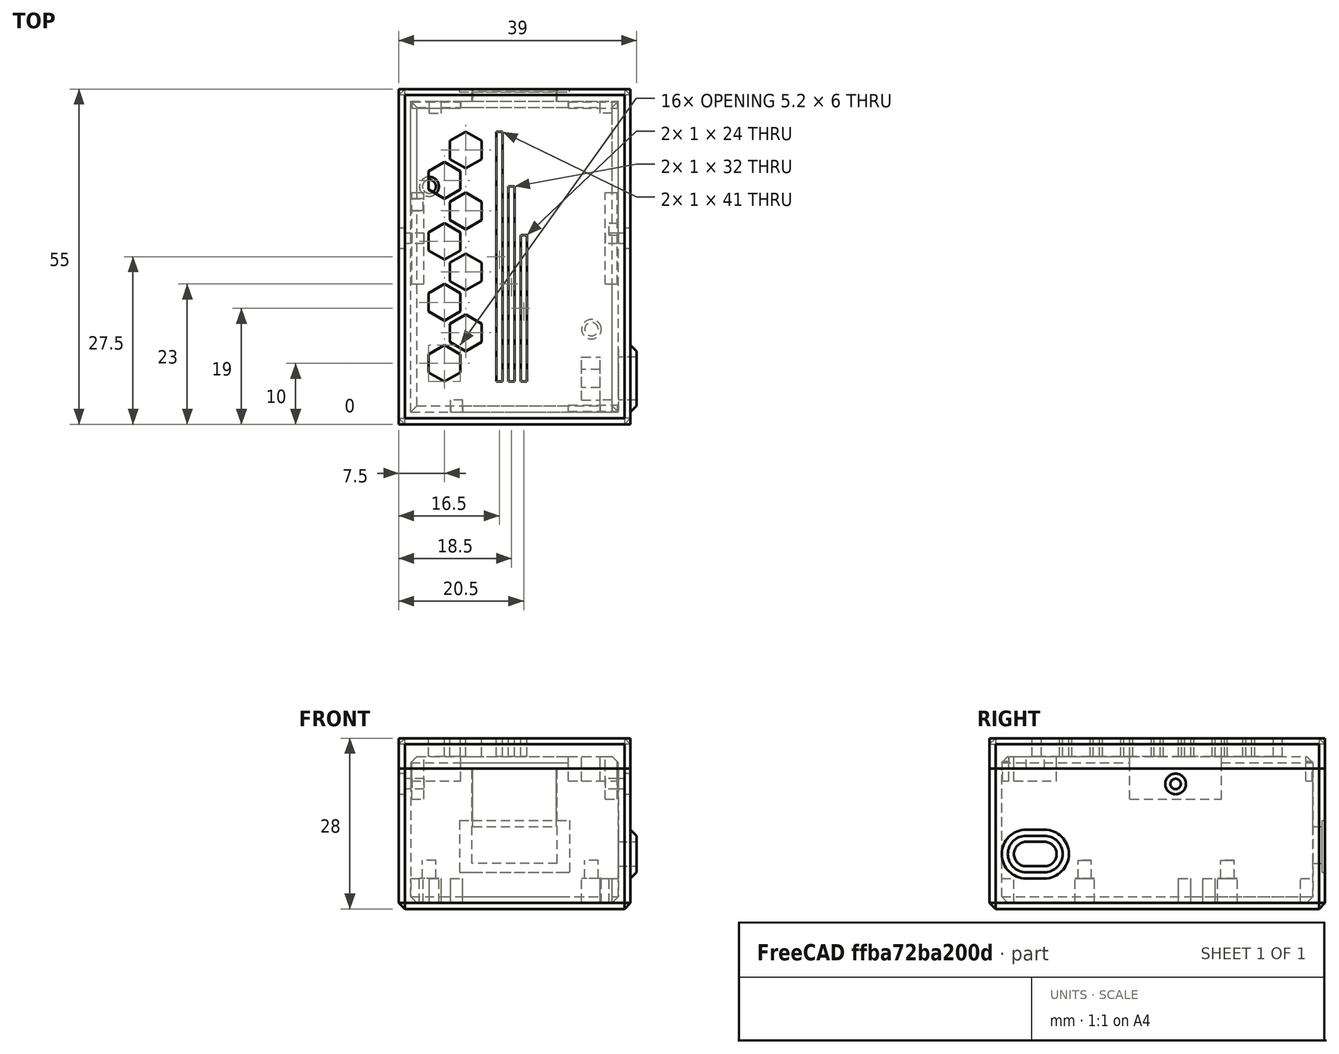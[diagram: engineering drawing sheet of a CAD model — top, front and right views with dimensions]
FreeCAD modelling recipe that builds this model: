
FCSTD DOCUMENT  (FreeCAD 0.18R16146 (Git))
Label: ac-dc5v-mounter
License: All rights reserved
LicenseURL: http://en.wikipedia.org/wiki/All_rights_reserved
objects: Part::Box×38, Part::MultiFuse×20, Part::Cylinder×13, Part::Feature×11, Part::Cut×9, Part::Chamfer×6
note: 97 computed .brp shape members not serialized (recipe doc carries the construction recipe); baked Part::Feature solids carry a one-line shape summary decoded from their .brp

FEATURE [Part::Box] Box  label="Cube"
  AttacherType = Attacher::AttachEngine3D
  Height = 1
  Length = 34
  Width = 51
FEATURE [Part::Box] Box001  label="Cube001"
  AttacherType = Attacher::AttachEngine3D
  Height = 5
  Length = 2
  Placement = pos=(6.5,0,0) rot=(0,0,1;0rad)
  Width = 2
FEATURE [Part::Box] Box002  label="Cube002"
  AttacherType = Attacher::AttachEngine3D
  Height = 5
  Length = 2
  Placement = pos=(0,33,0) rot=(0,0,1;0rad)
  Width = 2
FEATURE [Part::Box] Box003  label="Cube003"
  AttacherType = Attacher::AttachEngine3D
  Height = 5
  Length = 2
  Placement = pos=(31,0,0) rot=(0,0,1;0rad)
  Width = 2
FEATURE [Part::Box] Box004  label="Cube004"
  AttacherType = Attacher::AttachEngine3D
  Height = 5
  Length = 2
  Placement = pos=(31,49,0) rot=(0,0,1;0rad)
  Width = 2
FEATURE [Part::Box] Box005  label="Cube005"
  AttacherType = Attacher::AttachEngine3D
  Height = 5
  Length = 2
  Placement = pos=(3,49,0) rot=(0,0,1;0rad)
  Width = 2
FEATURE [Part::Box] Box006  label="Cube006"
  AttacherType = Attacher::AttachEngine3D
  Height = 5
  Length = 1.5
  Placement = pos=(32.5,29,0) rot=(0,0,1;0rad)
  Width = 2
FEATURE [Part::Box] Box007  label="Cube007"
  AttacherType = Attacher::AttachEngine3D
  Height = 23
  Length = 2
  Placement = pos=(-2,-2,0) rot=(0,0,1;0rad)
  Width = 55
FEATURE [Part::MultiFuse] Fusion
  Shapes = -> [Box006,Box005,Box004,Box003,Box002,Box001]
FEATURE [Part::Box] Box008  label="Cube008"
  AttacherType = Attacher::AttachEngine3D
  Height = 23
  Length = 38
  Placement = pos=(-2,-2,0) rot=(0,0,1;0rad)
  Width = 2
FEATURE [Part::Box] Box009  label="Cube009"
  AttacherType = Attacher::AttachEngine3D
  Height = 23
  Length = 12
  Placement = pos=(-2,51,0) rot=(0,0,1;0rad)
  Width = 2
FEATURE [Part::Box] Box010  label="Cube010"
  AttacherType = Attacher::AttachEngine3D
  Height = 23
  Length = 2
  Placement = pos=(34,-2,0) rot=(0,0,1;0rad)
  Width = 55
FEATURE [Part::Cylinder] Cylinder
  Angle = 360
  AttacherType = Attacher::AttachEngine3D
  Height = 5
  Placement = pos=(3,37,0) rot=(0,0,1;0rad)
  Radius = 1.6
FEATURE [Part::Cylinder] Cylinder001
  Angle = 360
  AttacherType = Attacher::AttachEngine3D
  Height = 5
  Placement = pos=(29.6,13.6,0) rot=(0,0,1;0rad)
  Radius = 1.6
FEATURE [Part::Cylinder] Cylinder002
  Angle = 360
  AttacherType = Attacher::AttachEngine3D
  Height = 8
  Placement = pos=(29.6,13.6,0) rot=(0,0,1;0rad)
  Radius = 1.1
FEATURE [Part::Cylinder] Cylinder003
  Angle = 360
  AttacherType = Attacher::AttachEngine3D
  Height = 8
  Placement = pos=(3,37,0) rot=(0,0,1;0rad)
  Radius = 1.1
FEATURE [Part::Box] Box011  label="Cube011"
  AttacherType = Attacher::AttachEngine3D
  Height = 23
  Length = 12
  Placement = pos=(24,51,0) rot=(0,0,1;0rad)
  Width = 2
FEATURE [Part::Box] Box012  label="Cube012"
  AttacherType = Attacher::AttachEngine3D
  Height = 7.5
  Length = 15
  Placement = pos=(9.5,51,0) rot=(0,0,1;0rad)
  Width = 2
FEATURE [Part::Box] Box013  label="Cube013"
  AttacherType = Attacher::AttachEngine3D
  Height = 8.5
  Length = 18
  Placement = pos=(8,52.5,6) rot=(0,0,1;0rad)
  Width = 2
FEATURE [Part::Box] Box014  label="Cube014"
  AttacherType = Attacher::AttachEngine3D
  Height = 2
  Length = 8
  Placement = pos=(0.15,49.85,25) rot=(0,0,1;0rad)
  Width = 1
FEATURE [Part::Box] Box015  label="Cube015"
  AttacherType = Attacher::AttachEngine3D
  Height = 2
  Length = 8
  Placement = pos=(25.85,49.85,25) rot=(0,0,1;0rad)
  Width = 1
FEATURE [Part::Box] Box016  label="Cube016"
  AttacherType = Attacher::AttachEngine3D
  Height = 5
  Length = 2
  Placement = pos=(0.15,21,22) rot=(0,0,1;0rad)
  Width = 15
FEATURE [Part::Box] Box017  label="Cube017"
  AttacherType = Attacher::AttachEngine3D
  Height = 5
  Length = 2
  Placement = pos=(31.85,21,22) rot=(0,0,1;0rad)
  Width = 15
FEATURE [Part::Box] Box018  label="Cube018"
  AttacherType = Attacher::AttachEngine3D
  Height = 2
  Length = 8
  Placement = pos=(25.85,0.15,25) rot=(0,0,1;0rad)
  Width = 1
FEATURE [Part::Box] Box020  label="Cube020"
  AttacherType = Attacher::AttachEngine3D
  Height = 11.5
  Length = 13.7
  Placement = pos=(10.15,51,13.5) rot=(0,0,1;0rad)
  Width = 2
FEATURE [Part::Box] Box021  label="Cube021"
  AttacherType = Attacher::AttachEngine3D
  Height = 1
  Length = 13.7
  Placement = pos=(10.15,52.5,13.5) rot=(0,0,1;0rad)
  Width = 0.5
FEATURE [Part::Cut] Cut001
  Base = -> Box020
  Placement = pos=(0,0,2) rot=(0,0,1;0rad)
  Tool = -> Box021
FEATURE [Part::MultiFuse] Fusion009
  Shapes = -> [Box011,Box009,Box010,Box007,Box008]
FEATURE [Part::MultiFuse] Fusion010
  Shapes = -> [Box012,Box,Fusion009]
FEATURE [Part::Cut] Cut
  Base = -> Fusion010
  Tool = -> Box013
FEATURE [Part::Chamfer] Chamfer
  Base = -> Cut
  Edges = 4 edges r=1: [Edge5,Edge9,Edge10,Edge11]
FEATURE [Part::Box] Box022  label="Cube022"
  AttacherType = Attacher::AttachEngine3D
  Height = 2
  Length = 2
  Placement = pos=(-2,-2,0) rot=(0,0,1;0rad)
  Width = 55
FEATURE [Part::Box] Box023  label="Cube023"
  AttacherType = Attacher::AttachEngine3D
  Height = 2
  Length = 2
  Placement = pos=(34,-2,0) rot=(0,0,1;0rad)
  Width = 55
FEATURE [Part::Box] Box024  label="Cube024"
  AttacherType = Attacher::AttachEngine3D
  Height = 2
  Length = 38
  Placement = pos=(-2,-2,0) rot=(0,0,1;0rad)
  Width = 2
FEATURE [Part::Box] Box025  label="Cube025"
  AttacherType = Attacher::AttachEngine3D
  Height = 2
  Length = 38
  Placement = pos=(-2,51,0) rot=(0,0,1;0rad)
  Width = 2
FEATURE [Part::MultiFuse] Fusion012
  Placement = pos=(0,0,25) rot=(0,0,1;0rad)
  Shapes = -> [Box025,Box024,Box023,Box022]
FEATURE [Part::Box] Box026  label="Cube026"
  AttacherType = Attacher::AttachEngine3D
  Height = 3
  Length = 38
  Placement = pos=(-2,-2,27) rot=(0,0,1;0rad)
  Width = 55
FEATURE [Part::MultiFuse] Fusion013
  Shapes = -> [Cut001,Box026,Fusion012]
FEATURE [Part::Box] Box027  label="Cube027"
  AttacherType = Attacher::AttachEngine3D
  Height = 2
  Length = 8
  Placement = pos=(25.85,0,25) rot=(0,0,1;0rad)
  Width = 1.15
FEATURE [Part::Box] Box028  label="Cube028"
  AttacherType = Attacher::AttachEngine3D
  Height = 2
  Length = 2.15
  Placement = pos=(0,21,25) rot=(0,0,1;0rad)
  Width = 15
FEATURE [Part::Box] Box029  label="Cube029"
  AttacherType = Attacher::AttachEngine3D
  Height = 2
  Length = 8
  Placement = pos=(25.85,49.85,25) rot=(0,0,1;0rad)
  Width = 1.15
FEATURE [Part::Box] Box030  label="Cube030"
  AttacherType = Attacher::AttachEngine3D
  Height = 2
  Length = 2.15
  Placement = pos=(31.85,21,25) rot=(0,0,1;0rad)
  Width = 15
FEATURE [Part::Box] Box031  label="Cube031"
  AttacherType = Attacher::AttachEngine3D
  Height = 2
  Length = 8
  Placement = pos=(0.15,49.85,25) rot=(0,0,1;0rad)
  Width = 1.15
FEATURE [Part::MultiFuse] Fusion014
  Shapes = -> [Box031,Box030,Box029,Box028,Box027]
FEATURE [Part::MultiFuse] Fusion016
  Placement = pos=(0,0,-2) rot=(0,0,1;0rad)
  Shapes = -> [Box018,Box016,Box015,Box017,Box014]
FEATURE [Part::Box] Box032  label="Cube032"
  AttacherType = Attacher::AttachEngine3D
  Height = 4
  Length = 3
  Width = 7
FEATURE [Part::Box] Box033  label="Cube033"
  AttacherType = Attacher::AttachEngine3D
  Height = 4
  Length = 3
  Placement = pos=(0,2,2) rot=(0,0,1;0rad)
  Width = 3
FEATURE [Part::Cut] Cut002
  Base = -> Box032
  Placement = pos=(28,2,23) rot=(0,0,1;0rad)
  Tool = -> Box033
FEATURE [Part::Cylinder] Cylinder004
  Angle = 360
  AttacherType = Attacher::AttachEngine3D
  Height = 10
  Placement = pos=(5,28.5,20.5) rot=(0,-1,0;1.5708rad)
  Radius = 0.85
FEATURE [Part::Cylinder] Cylinder005
  Angle = 360
  AttacherType = Attacher::AttachEngine3D
  Height = 10
  Placement = pos=(38,28.5,20.5) rot=(0,-1,0;1.5708rad)
  Radius = 0.85
FEATURE [Part::Cylinder] Cylinder006
  Angle = 360
  AttacherType = Attacher::AttachEngine3D
  Height = 1
  Placement = pos=(36,28.5,20.5) rot=(0,-1,0;1.5708rad)
  Radius = 1.7
FEATURE [Part::Cylinder] Cylinder007
  Angle = 360
  AttacherType = Attacher::AttachEngine3D
  Height = 1
  Placement = pos=(-1,28.5,20.5) rot=(0,-1,0;1.5708rad)
  Radius = 1.7
FEATURE [Part::MultiFuse] Fusion019
  Shapes = -> [Cylinder005,Cylinder004]
FEATURE [Part::Cylinder] Cylinder008
  Angle = 360
  AttacherType = Attacher::AttachEngine3D
  Height = 10
  Placement = pos=(38,28.5,20.5) rot=(0,-1,0;1.5708rad)
  Radius = 0.85
FEATURE [Part::Cylinder] Cylinder009
  Angle = 360
  AttacherType = Attacher::AttachEngine3D
  Height = 10
  Placement = pos=(5,28.5,20.5) rot=(0,-1,0;1.5708rad)
  Radius = 0.85
FEATURE [Part::MultiFuse] Fusion020
  Shapes = -> [Cylinder009,Cylinder008]
FEATURE [Part::MultiFuse] Fusion021
  Shapes = -> [Cylinder006,Cylinder007]
FEATURE [Part::Feature] Body001
  Placement = pos=(19,8,20) rot=(0,0,-1;1.5708rad)
  shape: bbox 5.196 x 6 x 10 mm, 8 faces (baked)
FEATURE [Part::Feature] Body002001  label="Body003"
  Placement = pos=(3.5,5,0) rot=(0,0,1;0rad)
  shape: bbox 5.196 x 6 x 10 mm, 8 faces (baked)
FEATURE [Part::Feature] Body001001  label="Body004"
  Placement = pos=(0,10,0) rot=(0,0,1;0rad)
  shape: bbox 5.196 x 6 x 10 mm, 8 faces (baked)
FEATURE [Part::Feature] Body002002  label="Body005"
  Placement = pos=(3.5,15,0) rot=(0,0,1;0rad)
  shape: bbox 5.196 x 6 x 10 mm, 8 faces (baked)
FEATURE [Part::Feature] Body002003  label="Body006"
  Placement = pos=(0,20,0) rot=(0,0,1;0rad)
  shape: bbox 5.196 x 6 x 10 mm, 8 faces (baked)
FEATURE [Part::Feature] Body002004  label="Body007"
  Placement = pos=(3.5,25,0) rot=(0,0,1;0rad)
  shape: bbox 5.196 x 6 x 10 mm, 8 faces (baked)
FEATURE [Part::Feature] Body002005  label="Body008"
  Placement = pos=(0,30,0) rot=(0,0,1;0rad)
  shape: bbox 5.196 x 6 x 10 mm, 8 faces (baked)
FEATURE [Part::Feature] Body002006  label="Body009"
  Placement = pos=(3.5,35,0) rot=(0,0,1;0rad)
  shape: bbox 5.196 x 6 x 10 mm, 8 faces (baked)
FEATURE [Part::MultiFuse] Fusion022
  Placement = pos=(-13.5,0,0) rot=(0,0,1;0rad)
  Shapes = -> [Body002006,Body002004,Body002003,Body002005,Body001001,Body002002,Body002001,Body001]
FEATURE [Part::MultiFuse] Fusion023
  Shapes = -> [Fusion016,Fusion014]
FEATURE [Part::Chamfer] Chamfer001
  Base = -> Fusion013
  Edges = 4 edges r=1: [Edge68,Edge72,Edge88,Edge89]
FEATURE [Part::MultiFuse] Fusion024
  Placement = pos=(0,0,-2) rot=(0,0,1;0rad)
  Shapes = -> [Chamfer001,Fusion023,Cut002]
FEATURE [Part::Cut] Cut006
  Base = -> Fusion024
  Tool = -> Fusion020
FEATURE [Part::Cut] Cut007
  Base = -> Cut006
  Tool = -> Fusion022
FEATURE [Part::Box] Box034  label="Cube034"
  AttacherType = Attacher::AttachEngine3D
  Height = 10
  Length = 1
  Placement = pos=(14,5,22) rot=(0,0,1;0rad)
  Width = 41
FEATURE [Part::Box] Box035  label="Cube035"
  AttacherType = Attacher::AttachEngine3D
  Height = 10
  Length = 1
  Placement = pos=(16,5,22) rot=(0,0,1;0rad)
  Width = 32
FEATURE [Part::Box] Box036  label="Cube036"
  AttacherType = Attacher::AttachEngine3D
  Height = 10
  Length = 1
  Placement = pos=(18,5,22) rot=(0,0,1;0rad)
  Width = 24
FEATURE [Part::MultiFuse] Fusion025
  Shapes = -> [Box036,Box035,Box034]
FEATURE [Part::Cut] Cut008
  Base = -> Cut007
  Tool = -> Fusion025
FEATURE [Part::Feature] Cut008001  label="Cut009"
  shape: bbox 38 x 55 x 14.5 mm, 125 faces (baked)
FEATURE [Part::Chamfer] Chamfer002  label="cap"
  Base = -> Cut008001
  Edges = 8 edges r=1: [Edge310,Edge311,Edge312,Edge313,Edge355,Edge356,Edge361,Edge363]
FEATURE [Part::Cylinder] Cylinder010
  Angle = 360
  AttacherType = Attacher::AttachEngine3D
  Height = 3
  Placement = pos=(37,4,19) rot=(0,-1,0;1.5708rad)
  Radius = 4
FEATURE [Part::Cylinder] Cylinder011
  Angle = 360
  AttacherType = Attacher::AttachEngine3D
  Height = 3
  Placement = pos=(37,4,9) rot=(0,-1,0;1.5708rad)
  Radius = 2
FEATURE [Part::Chamfer] Chamfer003
  Base = -> Cylinder010
  Edges = 1 edges r=1: [Edge3]
  Placement = pos=(0,0,-10) rot=(0,0,1;0rad)
FEATURE [Part::Feature] Chamfer002001  label="cap001"
  shape: bbox 38 x 55 x 14.5 mm, 137 faces (baked)
FEATURE [Part::Feature] Chamfer003001  label="Chamfer004"
  Placement = pos=(0,3,-10) rot=(0,0,1;0rad)
  shape: bbox 3 x 8 x 8 mm, 4 faces (baked)
FEATURE [Part::Cylinder] Cylinder012
  Angle = 360
  AttacherType = Attacher::AttachEngine3D
  Height = 3
  Placement = pos=(37,7,9) rot=(0,-1,0;1.5708rad)
  Radius = 2
FEATURE [Part::Box] Box037  label="Cube037"
  AttacherType = Attacher::AttachEngine3D
  Height = 8
  Length = 3
  Placement = pos=(34,4,5) rot=(0,0,1;0rad)
  Width = 3
FEATURE [Part::Chamfer] Chamfer003002
  Base = -> Box037
  Edges = 2 edges r=1: [Edge6,Edge8]
FEATURE [Part::Box] Box038  label="Cube038"
  AttacherType = Attacher::AttachEngine3D
  Height = 4
  Length = 3
  Placement = pos=(34,4,7) rot=(0,0,1;0rad)
  Width = 3
FEATURE [Part::MultiFuse] Fusion026
  Shapes = -> [Chamfer003001,Chamfer003002,Chamfer003]
FEATURE [Part::MultiFuse] Fusion027
  Shapes = -> [Box038,Cylinder012,Cylinder011]
FEATURE [Part::MultiFuse] Fusion028
  Shapes = -> [Cylinder001,Cylinder,Cylinder002,Cylinder003]
FEATURE [Part::MultiFuse] Fusion029
  Shapes = -> [Chamfer,Fusion028]
FEATURE [Part::MultiFuse] Fusion030
  Shapes = -> [Fusion029,Fusion]
FEATURE [Part::Cut] Cut008002
  Base = -> Fusion030
  Tool = -> Fusion019
FEATURE [Part::Cut] Cut008003
  Base = -> Cut008002
  Tool = -> Fusion021
FEATURE [Part::MultiFuse] Fusion031
  Shapes = -> [Cut008003,Fusion026]
FEATURE [Part::Cut] Cut008004
  Base = -> Fusion031
  Tool = -> Fusion027
FEATURE [Part::Chamfer] Chamfer003003
  Base = -> Cut008004
  Edges = 8 edges r=1: [Edge201,Edge205,Edge234,Edge243,Edge280,Edge289,Edge294,Edge331]
